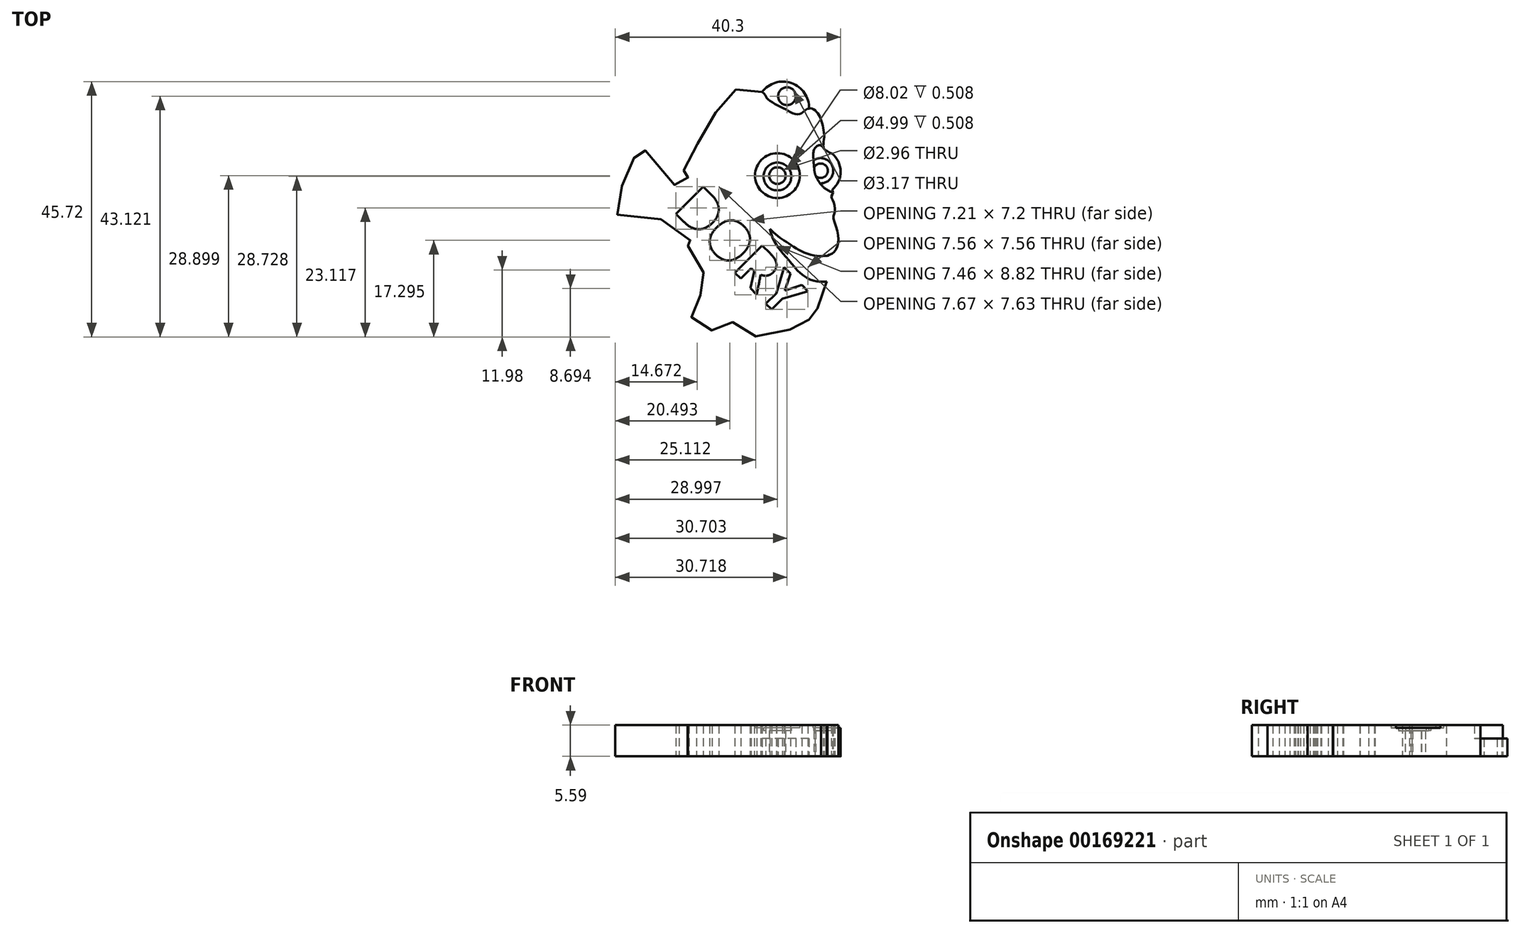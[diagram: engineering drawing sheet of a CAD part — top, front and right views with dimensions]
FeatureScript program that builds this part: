
annotation { "Feature Type Name" : "Feature", "Feature Type Description" : "" }
export const myFeature = defineFeature(function(context is Context, id is Id, definition is map)
    precondition{}
    {
        {
            var Q0;
            Q0=qCreatedBy(makeId("Top.planeOp"),FACE);
            var sketch = newSketch(context, id + "F0", { "sketchPlane" : qUnion([Q0])});
            skFitSpline(sketch, "E0", {"points": [v(10.83, 16.93) * mm, v(9.77, 16.44) * mm, v(8.85, 15.86) * mm, v(7.5, 16.2) * mm, v(6, 17.03) * mm, v(3.96, 18.1) * mm, v(3.04, 18.91) * mm, v(2.75, 19.45) * mm, v(1.34, 20.46) * mm, v(-0.06, 20.9) * mm, v(-1.85, 20.51) * mm, v(-3.35, 19.74) * mm, v(-4.9, 18) * mm, v(-6.11, 16.1) * mm, v(-7.52, 13.93) * mm, v(-9.02, 11.07) * mm, v(-10.18, 8.7) * mm, v(-11.05, 6.76) * mm, v(-11.83, 5.74) * mm, v(-12.55, 4.53) * mm, v(-12.36, 4.24) * mm, v(-11.92, 4.34) * mm, v(-11.24, 4.68) * mm, v(-10.8, 4.24) * mm, v(-11.15, 3.56) * mm, v(-11.73, 3.08) * mm, v(-12.9, 2.98) * mm, v(-14.25, 3.95) * mm, v(-17.5, 7.58) * mm, v(-19.67, 10.83) * mm, v(-19.96, 10.4) * mm, v(-20.2, 8.9) * mm, v(-21.27, 7.24) * mm, v(-22.1, 5.6) * mm, v(-22.77, 3.27) * mm, v(-23.01, 0.51) * mm, v(-23.98, -1.95) * mm, v(-23.6, -2.1) * mm, v(-19.28, -2.25) * mm, v(-15.26, -3.07) * mm, v(-12.84, -3.94) * mm, v(-10.57, -6.7) * mm, v(-9.45, -8.59) * mm, v(-9.74, -8.68) * mm, v(-10.28, -8.3) * mm, v(-11, -7.72) * mm, v(-10.95, -8.25) * mm, v(-9.94, -9.85) * mm, v(-7.8, -13.04) * mm, v(-6.7, -15.37) * mm, v(-7.47, -15.9) * mm, v(-9.89, -17.16) * mm, v(-10.95, -18.47) * mm, v(-10.71, -19.97) * mm, v(-9.6, -20.98) * mm, v(-7.95, -21.95) * mm, v(-7.32, -22.58) * mm, v(-6.65, -22.82) * mm, v(-5.63, -22.53) * mm, v(-4.51, -21.95) * mm, v(-3.3, -21.32) * mm, v(-2.63, -21.61) * mm, v(-1.66, -22.92) * mm, v(0.23, -23.74) * mm, v(3.14, -23.98) * mm, v(6.38, -23.26) * mm, v(7.69, -22.3) * mm, v(9.53, -20.93) * mm, v(10.01, -20.26) * mm, v(10.74, -20.98) * mm, v(11.95, -21.18) * mm, v(12.72, -20.79) * mm, v(12.58, -19.39) * mm, v(11.75, -18.13) * mm, v(12.58, -16.53) * mm, v(13.84, -14.01) * mm, v(13.98, -12.7) * mm, v(13.93, -11.4) * mm, v(13.5, -10.33) * mm, v(13.98, -10.04) * mm, v(13.98, -9.46) * mm, v(14.9, -9.02) * mm, v(15.72, -7.76) * mm, v(15.82, -5.4) * mm, v(15.05, -2.63) * mm, v(15.24, -1.8) * mm, v(15.24, -0.5) * mm, v(14.85, 0.66) * mm, v(14.7, 1.29) * mm, v(15, 1.82) * mm, v(14.85, 2.2) * mm, v(15.63, 3.27) * mm, v(16.3, 5.21) * mm, v(16.01, 7.2) * mm, v(14.8, 8.8) * mm, v(13.35, 9.71) * mm, v(13.35, 11.5) * mm, v(13.06, 14.17) * mm, v(12.1, 16.25) * mm, v(10.83, 16.93) * mm]});
            skCircle(sketch, "E1", {"center": v(5.02, 4.9) * mm, "radius": 4.01 * mm});
            skFitSpline(sketch, "E2", {"points": [v(13.35, 9.71) * mm, v(12.59, 10.35) * mm, v(11.67, 9.71) * mm, v(11.44, 8.36) * mm, v(11.59, 6.24) * mm, v(11.9, 4.78) * mm, v(13.35, 2.74) * mm, v(15, 1.82) * mm], "startDerivative": vector(-6.19, 8.28) * mm, "endDerivative": vector(10.82, -4.46) * mm});
            skArc(sketch, "E3", {"start": v(11.9, 4.8) * mm, "mid": v(14.01, 6.02) * mm, "end": v(11.58, 6.33) * mm});
            skArc(sketch, "E4", {"start": v(12.65, 3.5) * mm, "mid": v(14.92, 6.39) * mm, "end": v(11.47, 7.64) * mm});
            skCircle(sketch, "E5", {"center": v(5.02, 4.9) * mm, "radius": 1.48 * mm});
            skCircle(sketch, "E6", {"center": v(5.02, 4.73) * mm, "radius": 2.5 * mm});
            skFitSpline(sketch, "E7", {"points": [v(13.98, -9.46) * mm, v(11.87, -9.46) * mm, v(9.03, -8.5) * mm, v(6.9, -7.16) * mm, v(5.16, -6) * mm, v(3.65, -4.63) * mm], "startDerivative": vector(-10.6, -0.88) * mm, "endDerivative": vector(-7.79, 7.7) * mm});
            skFitSpline(sketch, "E8", {"points": [v(3.65, -4.63) * mm, v(4.61, -7.16) * mm, v(6.87, -10.04) * mm, v(9.89, -13.19) * mm, v(12.49, -14.11) * mm, v(13.84, -14.01) * mm], "startDerivative": vector(3.78, -13.24) * mm, "endDerivative": vector(9.01, 1.53) * mm});
            skArc(sketch, "E9", {"start": v(10.68, 16.92) * mm, "mid": v(7.55, 21.45) * mm, "end": v(2.27, 19.88) * mm});
            skCircle(sketch, "E10", {"center": v(6.74, 19.12) * mm, "radius": 1.59 * mm});
            skText(sketch, "E11", { "text": "DORY", "fontName": "OpenSans-Bold.ttf"});
            const initialGuessF0  = {"E11": [-0.01376, -0.00135, 0.7071, -0.7071, 0.00699]};
            skSetInitialGuess(sketch, initialGuessF0);
            skSolve(sketch);
        }
        {
            var Q0;
            Q0=makeQuery(id+"F0.imprint","IMPRINT",FACE,{"disambiguationData":[TD([[makeQuery(id+"F0.imprint","IMPRINT",EDGE,{"derivedFrom":sQuery(id+"F0.wireOp",EDGE,"E1")}),-1.0]])]});
            extrude(context, id + "F1", {"entities" : qUnion([Q0]), "depth" : 5.6 * mm});
        }
        {
            var Q0;
            Q0=makeQuery(id+"F0.imprint","IMPRINT",FACE,{"disambiguationData":[TD([[makeQuery(id+"F0.imprint","IMPRINT",EDGE,{"derivedFrom":sQuery(id+"F0.wireOp",EDGE,"E1")}),1.0]])]});
            var Q1;
            {var subQ4=sQuery(id+"F0.wireOp",EDGE,"E4");Q1=makeQuery(id+"F0.imprint","IMPRINT",FACE,{"disambiguationData":[TD([[makeQuery(id+"F0.imprint","IMPRINT",EDGE,{"derivedFrom":subQ4}),-1.0]])]});}
            extrude(context, id + "F2", {"entities" : qUnion([Q0, Q1]), "operationType" : NewBodyOperationType.ADD, "depth" : 5.08 * mm});
        }
        {
            var Q0;
            Q0=makeQuery(id+"F0.imprint","IMPRINT",FACE,{"disambiguationData":[TD([[makeQuery(id+"F0.imprint","IMPRINT",EDGE,{"derivedFrom":sQuery(id+"F0.wireOp",EDGE,"E5")}),-1.0]])]});
            var Q1;
            {var subQ0=sQuery(id+"F0.wireOp",EDGE,"E3");Q1=makeQuery(id+"F0.imprint","IMPRINT",FACE,{"disambiguationData":[TD([[makeQuery(id+"F0.imprint","IMPRINT",EDGE,{"derivedFrom":subQ0}),-1.0]])]});}
            extrude(context, id + "F3", {"entities" : qUnion([Q0, Q1]), "operationType" : NewBodyOperationType.ADD, "depth" : 4.57 * mm});
        }
        {
            var Q0;
            {var subQ0=sQuery(id+"F0.wireOp",EDGE,"E9");Q0=makeQuery(id+"F0.imprint","IMPRINT",FACE,{"disambiguationData":[TD([[makeQuery(id+"F0.imprint","IMPRINT",EDGE,{"derivedFrom":subQ0}),1.0]])]});}
            extrude(context, id + "F4", {"entities" : qUnion([Q0]), "operationType" : NewBodyOperationType.ADD, "depth" : 3.17 * mm});
        }
    });
